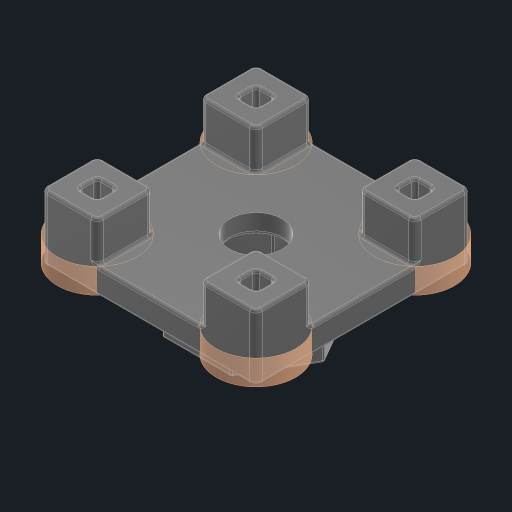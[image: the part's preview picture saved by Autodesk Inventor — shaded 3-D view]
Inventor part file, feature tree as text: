
AUTODESK INVENTOR PART (.ipt)
format: ipt  version: 2023 (Build 270158030, 158C)  size: 433,664 bytes
history: native  units: in
note: dims shown in document units (in); Inventor stores cm internally (conversion verified against a paired STEP export)
features: extrude x5, other x4, sketch x2, pattern_linear x1, projected_geometry x1, fillet x1
ambient origin geometry x8: Origin, YZ Plane, XZ Plane, XY Plane, X Axis, Y Axis, Z Axis, Center Point
bodies: Solid1 (feature_tree)
feature tree (14):
  pattern_linear  "Rectangular Pattern1"  Count1=2 Spacing1=0.5in
  extrude  "Extrusion1"  Depth=0.3937in TaperAngle=0.0deg
  sketch  "Sketch1"  dims[d0=0.25in]
  projected_geometry  "Projected Loop1"
  other  "Srf1"
  other  "Srf2"
  other  "Srf3"
  other  "Srf4"
  sketch  "Sketch2"  dims[d1=0.3937in d2=0.0in d3=0.7874in d5=0.5in d6=0.7874in d8=0.5in d9=0.3937in d10=0.0in]
  fillet  "Fillet10"  [1 undecoded]
  extrude  "ExtrusionSrf1"  [1 undecoded]
  extrude  "ExtrusionSrf2"  [1 undecoded]
  extrude  "ExtrusionSrf3"  [1 undecoded]
  extrude  "ExtrusionSrf4"  [1 undecoded]
note: 5 required parameter values undecoded (feature->parameter linkage not recoverable at this tier; creation-order binding heuristic only, values carry confidence <= 0.55)
